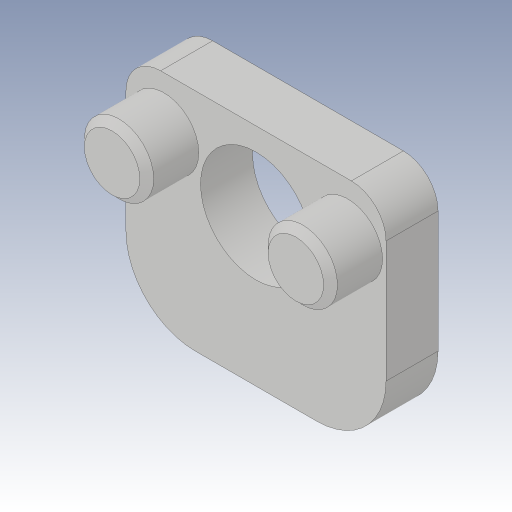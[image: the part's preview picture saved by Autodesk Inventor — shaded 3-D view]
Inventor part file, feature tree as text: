
AUTODESK INVENTOR PART (.ipt)
format: ipt  version: 2023.2 (Build 272271030, 271C)  size: 165,888 bytes
history: native  units: in
note: dims shown in document units (in); Inventor stores cm internally (conversion verified against a paired STEP export)
features: extrude x2, sketch x1, chamfer x1, fillet x1
ambient origin geometry x8: Origin, YZ Plane, XZ Plane, XY Plane, X Axis, Y Axis, Z Axis, Center Point
bodies: Body1 (feature_tree)
feature tree (5):
  sketch  "Skizze3"  dims[d4=0.2953in d5=0.2559in d6=0.0787in d7=0.0591in d8=0.0787in d9=0.0787in d10=0.0433in d11=0.0433in d13=0.126in d14=0.0886in d15=0.0591in d16=0.0in d17=0.0591in d18=0.0in d19=0.0079in d20=0.0787in d21=45.0deg d22=0.0394in]
  extrude  "Extrusion3"  Depth=0.2559in
  extrude  "Extrusion4"  Depth=0.0787in
  chamfer  "Fase1"  Distance=0.0591in
  fillet  "Rundung1"  Radius=0.0787in
